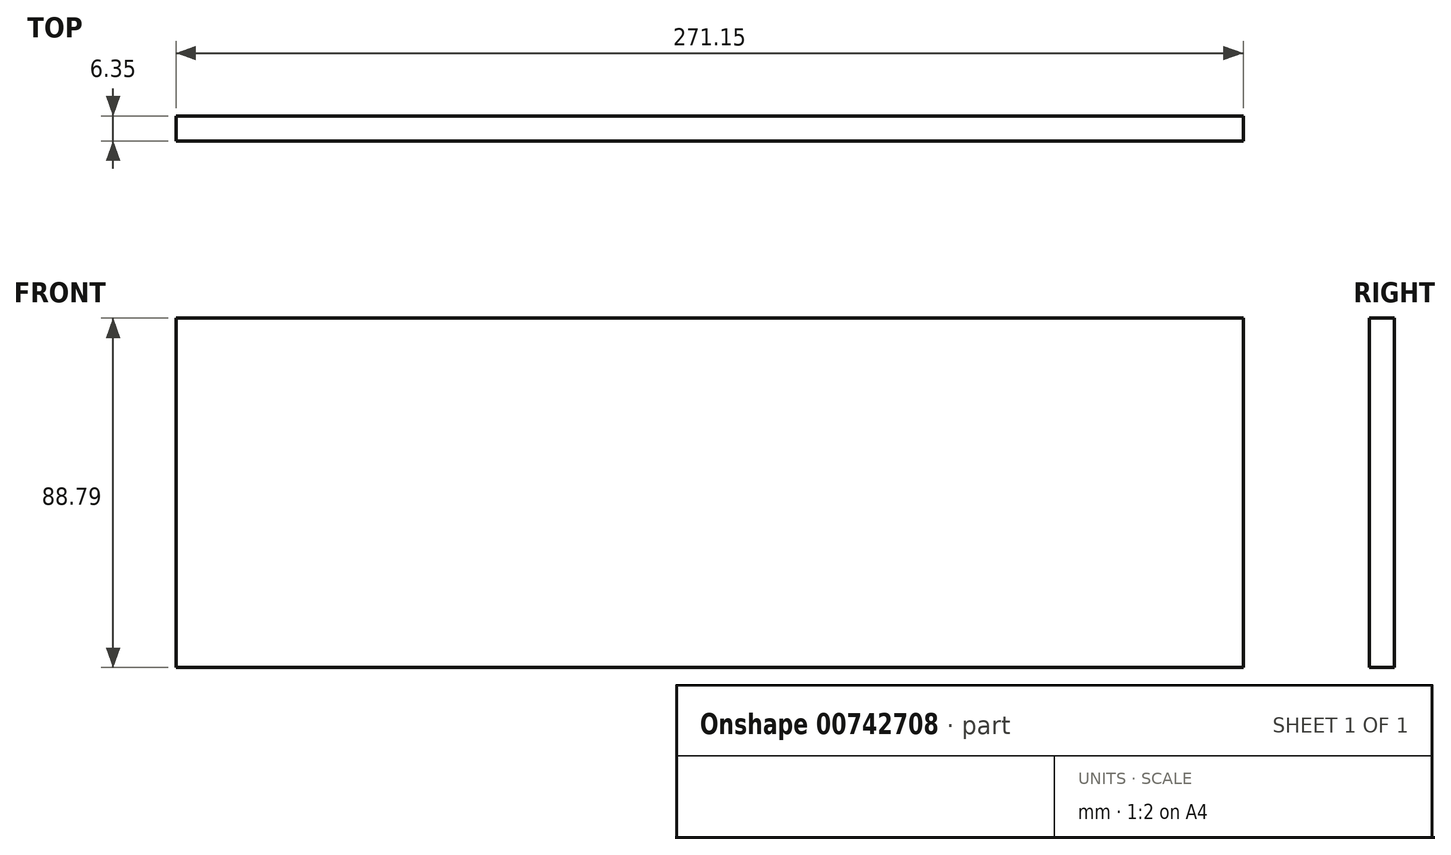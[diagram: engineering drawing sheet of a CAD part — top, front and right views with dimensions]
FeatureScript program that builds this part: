
annotation { "Feature Type Name" : "Feature", "Feature Type Description" : "" }
export const myFeature = defineFeature(function(context is Context, id is Id, definition is map)
    precondition{}
    {
        {
            var Q0;
            Q0=qCreatedBy(makeId("Front.planeOp"),FACE);
            var sketch = newSketch(context, id + "F0", { "sketchPlane" : qUnion([Q0])});
            skLineSegment(sketch, "E0.bottom", {"start": v(-125.92, 94.17) * mm, "end": v(145.23, 94.17) * mm});
            skLineSegment(sketch, "E0.top", {"start": v(-125.92, 5.38) * mm, "end": v(145.23, 5.38) * mm});
            skLineSegment(sketch, "E0.left", {"start": v(-125.92, 94.17) * mm, "end": v(-125.92, 5.38) * mm});
            skLineSegment(sketch, "E0.right", {"start": v(145.23, 94.17) * mm, "end": v(145.23, 5.38) * mm});
            skSolve(sketch);
        }
        {
            var Q0;
            Q0 = qSketchRegion(id + "F0", true);
            extrude(context, id + "F1", {"entities" : qUnion([Q0]), "depth" : 6.35 * mm, "offsetDistance" : 25.4 * mm});
        }
    });
